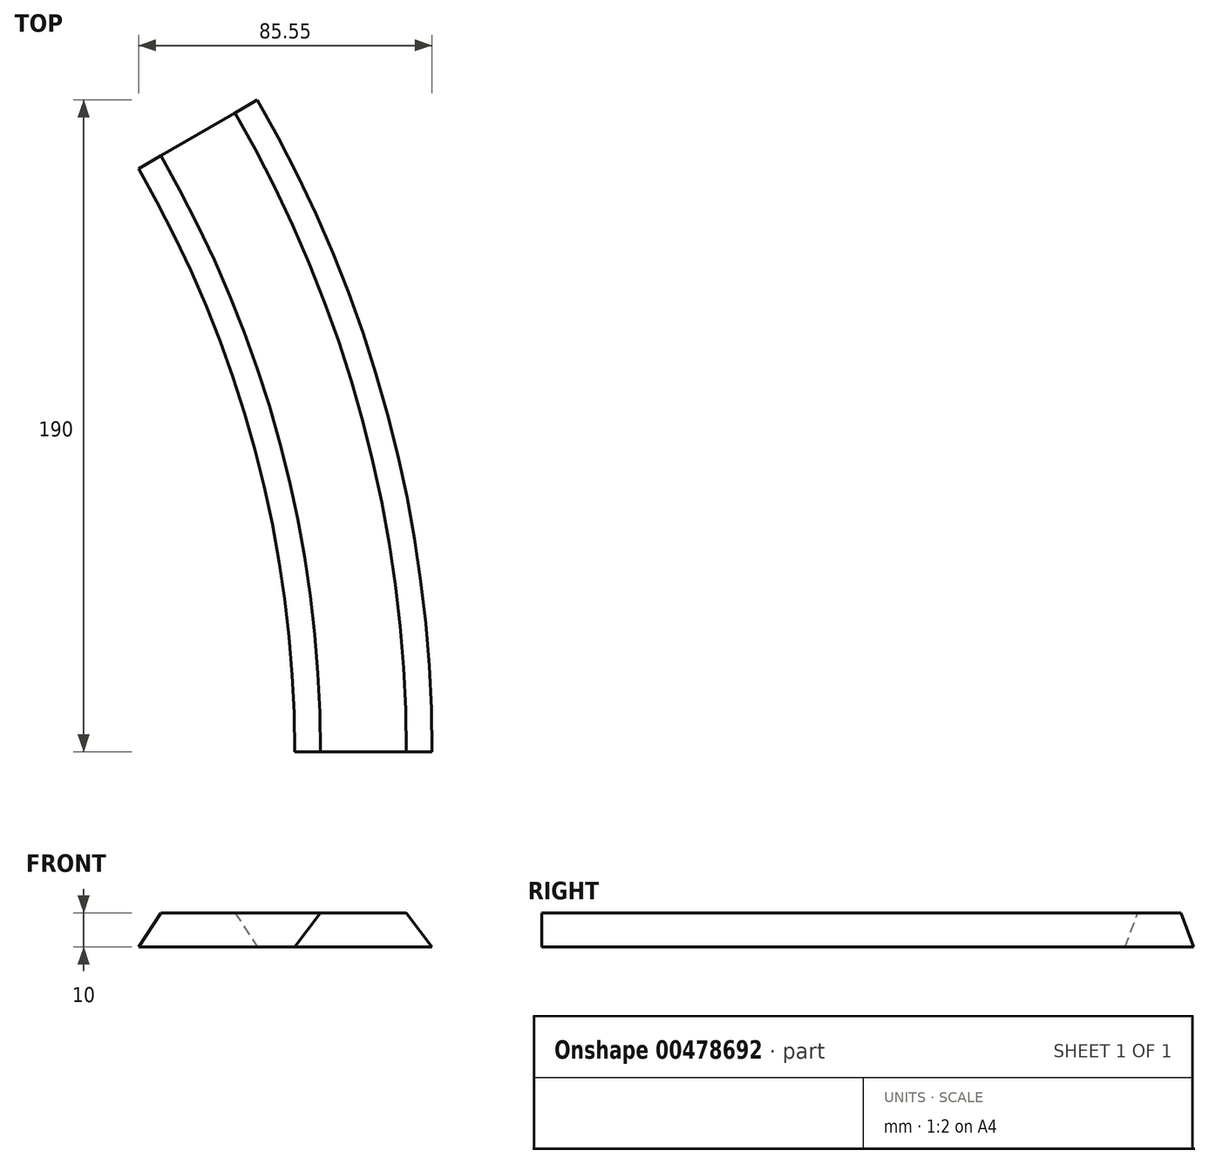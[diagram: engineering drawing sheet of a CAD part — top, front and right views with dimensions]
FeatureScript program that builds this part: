
annotation { "Feature Type Name" : "Feature", "Feature Type Description" : "" }
export const myFeature = defineFeature(function(context is Context, id is Id, definition is map)
    precondition{}
    {
        {
            var Q0;
            Q0=qCreatedBy(makeId("Front.planeOp"),FACE);
            var sketch = newSketch(context, id + "F0", { "sketchPlane" : qUnion([Q0])});
            skLineSegment(sketch, "E0", {"start": v(-20, 0) * mm, "end": v(-12.5, 10) * mm});
            skLineSegment(sketch, "E1", {"start": v(-12.5, 10) * mm, "end": v(12.5, 10) * mm});
            skLineSegment(sketch, "E2", {"start": v(12.5, 10) * mm, "end": v(20, 0) * mm});
            skLineSegment(sketch, "E3", {"start": v(20, 0) * mm, "end": v(-20, 0) * mm});
            skLineSegment(sketch, "E4", {"start": v(0, 0) * mm, "end": v(0, 30.14) * mm, "construction": true});
            skSolve(sketch);
        }
        {
            var Q0;
            Q0=qCreatedBy(makeId("Top.planeOp"),FACE);
            var sketch = newSketch(context, id + "F1", { "sketchPlane" : qUnion([Q0])});
            skArc(sketch, "E5", {"start": v(0, 0) * mm, "mid": v(-12.27, 93.17) * mm, "end": v(-48.23, 180) * mm});
            skLineSegment(sketch, "E6", {"start": v(-360, 0) * mm, "end": v(-48.23, 180) * mm, "construction": true});
            skLineSegment(sketch, "E7", {"start": v(-360, 0) * mm, "end": v(0, 0) * mm, "construction": true});
            skSolve(sketch);
        }
        {
            var Q0;
            Q0 = qSketchRegion(id + "F0", true);
            var Q1;
            Q1 = qConstructionFilter(qBodyType(qCreatedBy(id + "F1" ,EDGE), BodyType.WIRE), ConstructionObject.NO);
            sweep(context, id + "F2", {"profiles" : qUnion([Q0]), "path" : qUnion([Q1])});
        }
    });
